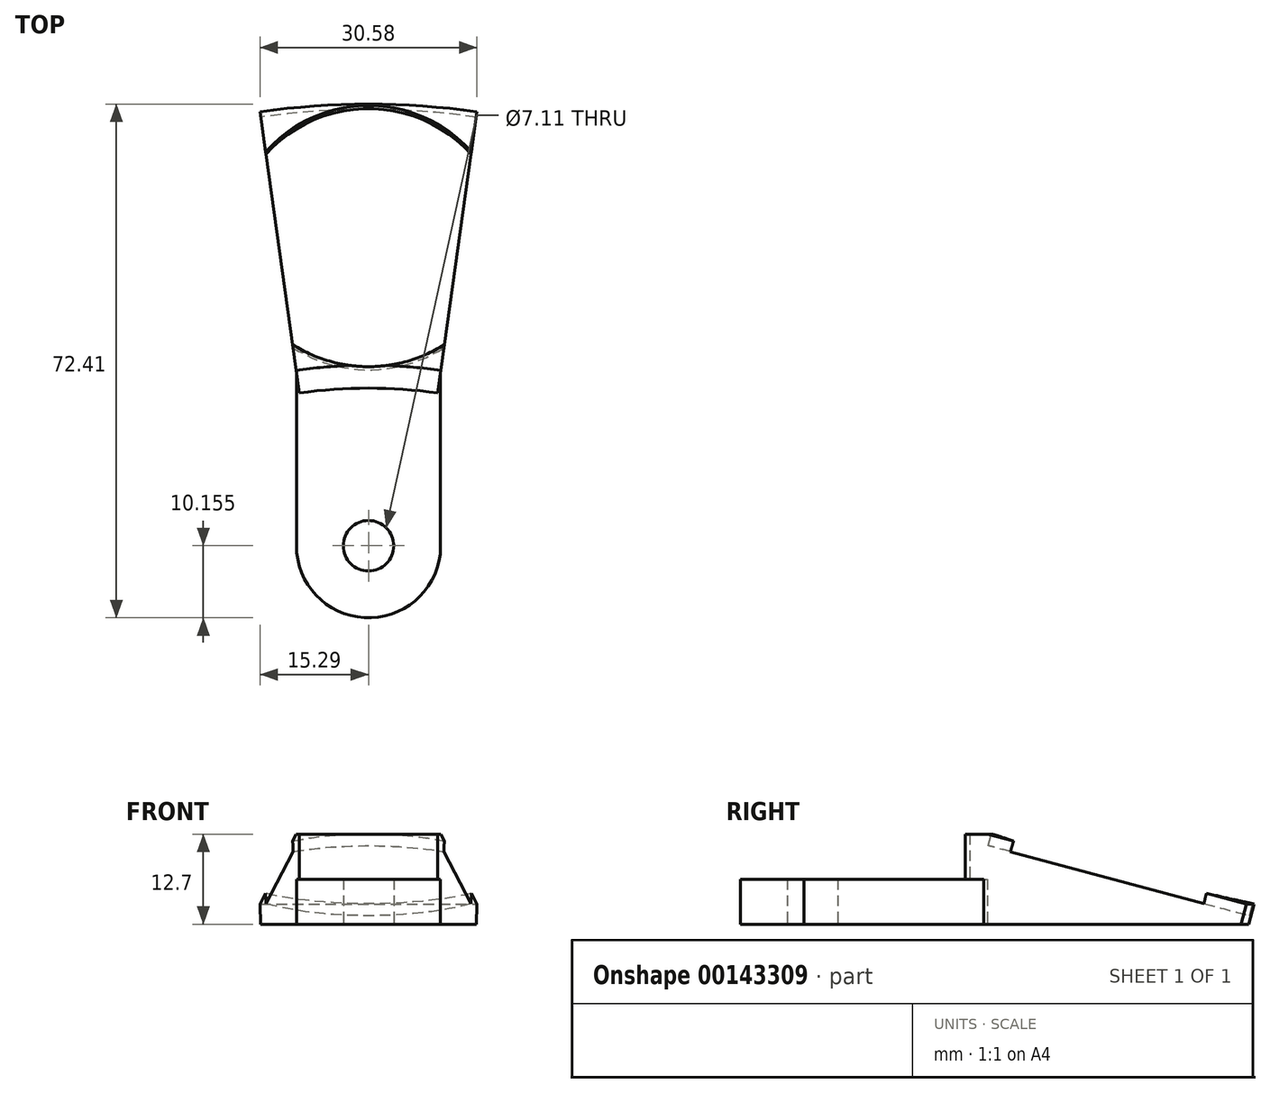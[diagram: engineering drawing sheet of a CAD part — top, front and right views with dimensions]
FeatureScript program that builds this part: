
annotation { "Feature Type Name" : "Feature", "Feature Type Description" : "" }
export const myFeature = defineFeature(function(context is Context, id is Id, definition is map)
    precondition{}
    {
        {
            var Q0;
            Q0=qCreatedBy(makeId("Top.planeOp"),FACE);
            var sketch = newSketch(context, id + "F0", { "sketchPlane" : qUnion([Q0])});
            skCircle(sketch, "E0", {"center": v(0, 0) * mm, "radius": 69.85 * mm});
            skLineSegment(sketch, "E1", {"start": v(0, 69.85) * mm, "end": v(0, 47.63) * mm});
            skCircle(sketch, "E2", {"center": v(0, 47.63) * mm, "radius": 3.56 * mm});
            skLineSegment(sketch, "E3", {"start": v(-10.16, 69.1) * mm, "end": v(-10.16, 47.63) * mm});
            skLineSegment(sketch, "E4", {"start": v(-10.16, 47.63) * mm, "end": v(-10.16, 69.1) * mm});
            skLineSegment(sketch, "E5", {"start": v(10.1, 69.1) * mm, "end": v(10.1, 46.46) * mm});
            skLineSegment(sketch, "E6", {"start": v(10.1, 46.46) * mm, "end": v(10.1, 69.1) * mm});
            skArc(sketch, "E7", {"start": v(-10.16, 47.63) * mm, "mid": v(-0.59, 37.48) * mm, "end": v(10.1, 46.46) * mm});
            skLineSegment(sketch, "E8", {"start": v(-10.16, 69.1) * mm, "end": v(-10.16, 88.16) * mm});
            skLineSegment(sketch, "E9", {"start": v(-10.16, 88.16) * mm, "end": v(10.1, 88.16) * mm});
            skLineSegment(sketch, "E10", {"start": v(10.1, 88.16) * mm, "end": v(10.1, 69.1) * mm});
            skSolve(sketch);
        }
        {
            var Q0;
            {var subQ1=sQuery(id+"F0.wireOp",EDGE,"E8");Q0=makeQuery(id+"F0.imprint","IMPRINT",FACE,{"disambiguationData":[TD([[makeQuery(id+"F0.imprint","IMPRINT",EDGE,{"derivedFrom":subQ1}),-1.0]])]});}
            var Q1;
            Q1=makeQuery(id+"F0.imprint","IMPRINT",FACE,{"disambiguationData":[TD([[makeQuery(id+"F0.imprint","IMPRINT",EDGE,{"derivedFrom":sQuery(id+"F0.wireOp",EDGE,"E2")}),-1.0]])]});
            extrude(context, id + "F1", {"entities" : qUnion([Q0, Q1]), "depth" : 6.35 * mm, "offsetDistance" : 25.4 * mm});
        }
        {
            var Q0;
            Q0=qCreatedBy(makeId("Right.planeOp"),FACE);
            var sketch = newSketch(context, id + "F2", { "sketchPlane" : qUnion([Q0])});
            skLineSegment(sketch, "E11", {"start": v(0, 0) * mm, "end": v(69.85, 0) * mm});
            skLineSegment(sketch, "E12", {"start": v(69.85, 0) * mm, "end": v(69.85, 6.35) * mm});
            skLineSegment(sketch, "E13", {"start": v(69.85, 6.35) * mm, "end": v(69.85, 12.7) * mm});
            skLineSegment(sketch, "E14", {"start": v(69.85, 12.7) * mm, "end": v(73.08, 12.7) * mm});
            skLineSegment(sketch, "E15", {"start": v(73.08, 12.7) * mm, "end": v(109.88, 2.84) * mm});
            skLineSegment(sketch, "E16", {"start": v(109.88, 2.84) * mm, "end": v(109.12, 0) * mm});
            skLineSegment(sketch, "E17", {"start": v(69.85, 0) * mm, "end": v(109.12, 0) * mm});
            skSolve(sketch);
        }
        {
            var Q0;
            Q0=makeQuery(id+"F2.imprint","IMPRINT",FACE,{"disambiguationData":[TD([[makeQuery(id+"F2.imprint","IMPRINT",EDGE,{"derivedFrom":sQuery(id+"F2.wireOp",EDGE,"E12")}),-1.0]])]});
            var Q1;
            Q1=sQuery(id+"F0.wireOp",EDGE,"E0");
            revolve(context, id + "F3", {"operationType" : NewBodyOperationType.ADD, "surfaceOperationType" : NewSurfaceOperationType.NEW, "entities" : qUnion([Q0]), "axis" : qUnion([Q1]), "revolveType" : RevolveType.TWO_DIRECTIONS, "angle" : 8 * degree, "angleBack" : 352 * degree});
        }
        {
            var Q0;
            Q0=qCreatedBy(makeId("Right.planeOp"),FACE);
            var sketch = newSketch(context, id + "F4", { "sketchPlane" : qUnion([Q0])});
            skLineSegment(sketch, "E18", {"start": v(89.19, 0) * mm, "end": v(90.83, 6.13) * mm});
            skLineSegment(sketch, "E19", {"start": v(90.83, 6.13) * mm, "end": v(89.19, 0) * mm});
            skLineSegment(sketch, "E20", {"start": v(89.19, 0) * mm, "end": v(0, 0) * mm});
            skLineSegment(sketch, "E21", {"start": v(90.83, 6.13) * mm, "end": v(109.23, 1.2) * mm});
            skLineSegment(sketch, "E22", {"start": v(109.23, 1.2) * mm, "end": v(110.05, 4.27) * mm});
            skLineSegment(sketch, "E23", {"start": v(110.05, 4.27) * mm, "end": v(73.25, 14.13) * mm});
            skLineSegment(sketch, "E24", {"start": v(73.25, 14.13) * mm, "end": v(72.43, 11.06) * mm});
            skLineSegment(sketch, "E25", {"start": v(72.43, 11.06) * mm, "end": v(90.83, 6.13) * mm});
            skLineSegment(sketch, "E26", {"start": v(90.83, 6.13) * mm, "end": v(91.65, 9.2) * mm});
            skSolve(sketch);
        }
        {
            var Q0;
            Q0=makeQuery(id+"F4.imprint","IMPRINT",FACE,{"disambiguationData":[TD([[makeQuery(id+"F4.imprint","IMPRINT",EDGE,{"derivedFrom":sQuery(id+"F4.wireOp",EDGE,"E21")}),1.0]])]});
            var Q1;
            Q1=sQuery(id+"F4.wireOp",EDGE,"E26");
            revolve(context, id + "F5", {"operationType" : NewBodyOperationType.REMOVE, "surfaceOperationType" : NewSurfaceOperationType.NEW, "entities" : qUnion([Q0]), "axis" : qUnion([Q1]), "revolveType" : RevolveType.FULL, "oppositeDirection" : true});
        }
    });
